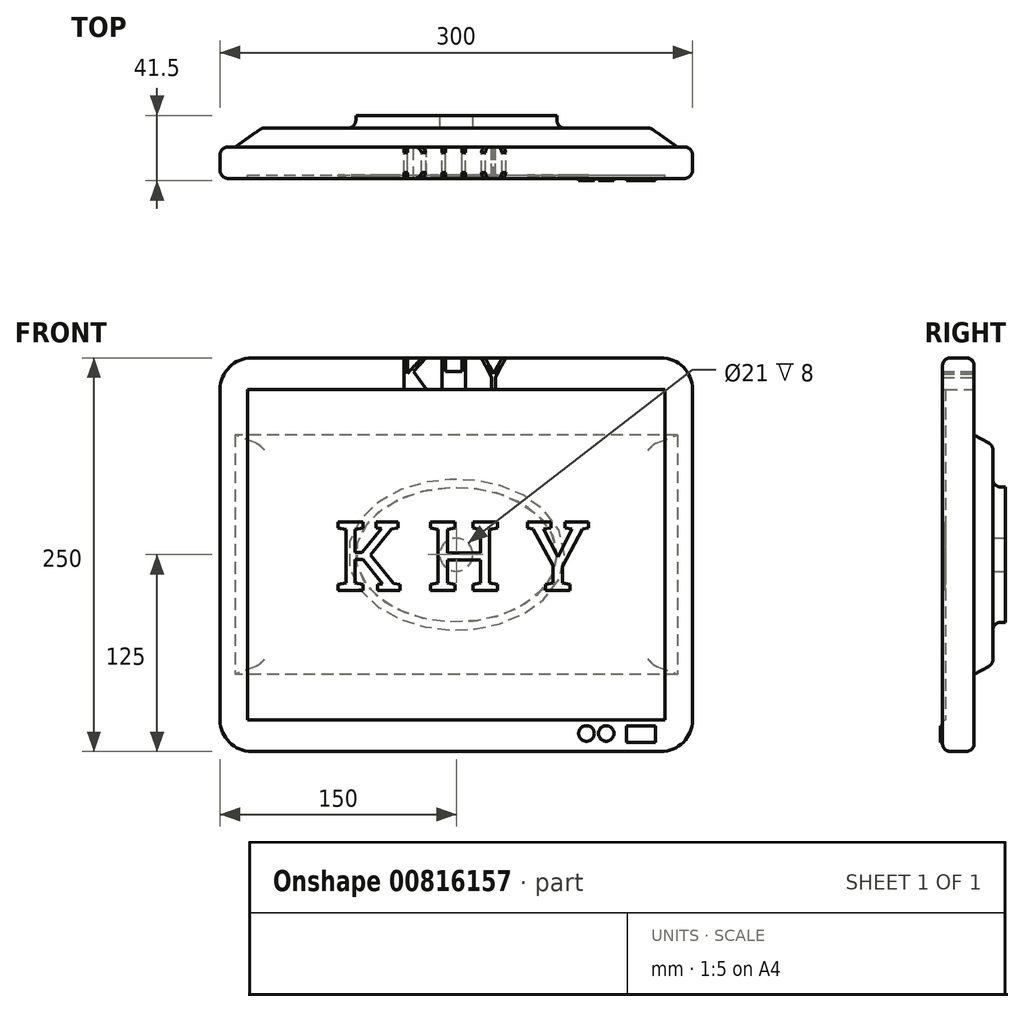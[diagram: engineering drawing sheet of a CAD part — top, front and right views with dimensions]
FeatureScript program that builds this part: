
annotation { "Feature Type Name" : "Feature", "Feature Type Description" : "" }
export const myFeature = defineFeature(function(context is Context, id is Id, definition is map)
    precondition{}
    {
        {
            var Q0;
            Q0=qCreatedBy(makeId("Front.planeOp"),FACE);
            var sketch = newSketch(context, id + "F0", { "sketchPlane" : qUnion([Q0])});
            skLineSegment(sketch, "E0.bottom", {"start": v(-130, 125) * mm, "end": v(130, 125) * mm});
            skLineSegment(sketch, "E0.top", {"start": v(-130, -125) * mm, "end": v(130, -125) * mm});
            skLineSegment(sketch, "E0.left", {"start": v(-150, 105) * mm, "end": v(-150, -105) * mm});
            skLineSegment(sketch, "E0.right", {"start": v(150, 105) * mm, "end": v(150, -105) * mm});
            skPoint(sketch, "E0.middle", {"position": v(0, 0) * mm});
            skLineSegment(sketch, "E1.bottom", {"start": v(-132.5, 105) * mm, "end": v(132.5, 105) * mm});
            skLineSegment(sketch, "E1.top", {"start": v(-132.5, -105) * mm, "end": v(132.5, -105) * mm});
            skLineSegment(sketch, "E1.left", {"start": v(-132.5, 105) * mm, "end": v(-132.5, -105) * mm});
            skLineSegment(sketch, "E1.right", {"start": v(132.5, 105) * mm, "end": v(132.5, -105) * mm});
            skPoint(sketch, "E2.visualSharp", {"position": v(-150, 125) * mm});
            skArc(sketch, "E2.filletArc", {"start": v(-130, 125) * mm, "mid": v(-144.14, 119.14) * mm, "end": v(-150, 105) * mm});
            skPoint(sketch, "E3.visualSharp", {"position": v(150, 125) * mm});
            skArc(sketch, "E3.filletArc", {"start": v(150, 105) * mm, "mid": v(144.14, 119.14) * mm, "end": v(130, 125) * mm});
            skPoint(sketch, "E4.visualSharp", {"position": v(-150, -125) * mm});
            skArc(sketch, "E4.filletArc", {"start": v(-150, -105) * mm, "mid": v(-144.14, -119.14) * mm, "end": v(-130, -125) * mm});
            skPoint(sketch, "E5.visualSharp", {"position": v(150, -125) * mm});
            skArc(sketch, "E5.filletArc", {"start": v(130, -125) * mm, "mid": v(144.14, -119.14) * mm, "end": v(150, -105) * mm});
            skText(sketch, "E6", { "text": "K H Y", "fontName": "OpenSans-Regular.ttf"});
            const initialGuessF0  = {"E6": [-0.0361, 0.105, 1, 0, 0.02]};
            skSetInitialGuess(sketch, initialGuessF0);
            skSolve(sketch);
        }
        {
            var Q0;
            Q0 = qSketchRegion(id + "F0", true);
            extrude(context, id + "F1", {"entities" : qUnion([Q0]), "depth" : 20 * mm, "offsetDistance" : 25 * mm});
        }
        {
            var Q0;
            Q0=makeQuery(id+"F0.imprint","IMPRINT",FACE,{"disambiguationData":[TD([[makeQuery(id+"F0.imprint","IMPRINT",EDGE,{"derivedFrom":sQuery(id+"F0.wireOp",EDGE,"E1.top")}),1.0]])]});
            extrude(context, id + "F2", {"entities" : qUnion([Q0]), "operationType" : NewBodyOperationType.ADD, "depth" : 18 * mm, "offsetDistance" : 25 * mm});
        }
        {
            var Q0;
            Q0=makeQuery(id+"F2.opExtrude","CAP_FACE",FACE,{"disambiguationData":[OSD([sQuery(id+"F0.wireOp",EDGE,"E1.bottom"),sQuery(id+"F0.wireOp",EDGE,"E1.top"),sQuery(id+"F0.wireOp",EDGE,"E1.left"),sQuery(id+"F0.wireOp",EDGE,"E1.right"),sQuery(id+"F0.wireOp",EDGE,"E6.sketch_text.stroke-0"),sQuery(id+"F0.wireOp",EDGE,"E6.sketch_text.stroke-4"),sQuery(id+"F0.wireOp",EDGE,"E6.sketch_text.stroke-12"),sQuery(id+"F0.wireOp",EDGE,"E6.sketch_text.stroke-16"),sQuery(id+"F0.wireOp",EDGE,"E6.sketch_text.stroke-28")])],"isStart":false});
            var sketch = newSketch(context, id + "F3", { "sketchPlane" : qUnion([Q0])});
            skText(sketch, "E7", { "text": " K H Y\n", "fontName": "RobotoSlab-Regular.ttf"});
            const initialGuessF3  = {"E7": [-0.09232, -0.02268, 1, 0, 0.044]};
            skSetInitialGuess(sketch, initialGuessF3);
            skSolve(sketch);
        }
        {
            var Q0;
            Q0 = qSketchRegion(id + "F3", true);
            extrude(context, id + "F4", {"entities" : qUnion([Q0]), "depth" : 0.5 * mm, "offsetDistance" : 25 * mm});
        }
        {
            var Q0;
            Q0=qCreatedBy(makeId("Front.planeOp"),FACE);
            cPlane(context, id + "F5", {"entities" : qUnion([Q0]), "cplaneType" : CPlaneType.OFFSET, "offset" : 12 * mm, "oppositeDirection" : true, "width" : 150 * mm, "height" : 150 * mm});
        }
        {
            var Q0;
            Q0=qCreatedBy(id+"F5.planeOp",FACE);
            var sketch = newSketch(context, id + "F6", { "sketchPlane" : qUnion([Q0])});
            skLineSegment(sketch, "E8.bottom", {"start": v(123.4, 69.44) * mm, "end": v(-123.4, 69.44) * mm});
            skLineSegment(sketch, "E8.top", {"start": v(123.4, -69.44) * mm, "end": v(-123.4, -69.44) * mm});
            skLineSegment(sketch, "E8.left", {"start": v(123.4, 69.44) * mm, "end": v(123.4, -69.44) * mm});
            skLineSegment(sketch, "E8.right", {"start": v(-123.4, 69.44) * mm, "end": v(-123.4, -69.44) * mm});
            skPoint(sketch, "E8.middle", {"position": v(0, 0) * mm});
            skSolve(sketch);
        }
        {
            var Q0;
            Q0=qCreatedBy(makeId("Front.planeOp"),FACE);
            var sketch = newSketch(context, id + "F7", { "sketchPlane" : qUnion([Q0])});
            skLineSegment(sketch, "E9.bottom", {"start": v(140.37, 75.91) * mm, "end": v(-140.37, 75.91) * mm});
            skLineSegment(sketch, "E9.top", {"start": v(140.37, -75.91) * mm, "end": v(-140.37, -75.91) * mm});
            skLineSegment(sketch, "E9.left", {"start": v(140.37, 75.91) * mm, "end": v(140.37, -75.91) * mm});
            skLineSegment(sketch, "E9.right", {"start": v(-140.37, 75.91) * mm, "end": v(-140.37, -75.91) * mm});
            skPoint(sketch, "E9.middle", {"position": v(0, 0) * mm});
            skSolve(sketch);
        }
        {
            var Q1;
            Q1=makeQuery(id+"F6.imprint","IMPRINT",FACE,{"disambiguationData":[TD([[makeQuery(id+"F6.imprint","IMPRINT",EDGE,{"derivedFrom":sQuery(id+"F6.wireOp",EDGE,"E8.bottom")}),1.0]])]});
            var Q2;
            Q2=makeQuery(id+"F7.imprint","IMPRINT",FACE,{"disambiguationData":[TD([[makeQuery(id+"F7.imprint","IMPRINT",EDGE,{"derivedFrom":sQuery(id+"F7.wireOp",EDGE,"E9.bottom")}),1.0]])]});
            loft(context, id + "F8", {"operationType" : NewBodyOperationType.ADD, "sheetProfilesArray" : [{ "sheetProfileEntities" : qUnion([Q1]) }, { "sheetProfileEntities" : qUnion([Q2]) }]});
        }
        {
            var Q0;
            Q0=makeQuery(id+"F8.opLoft","CAP_FACE",FACE,{"disambiguationData":[OSD([makeQuery(id+"F6.imprint","IMPRINT",FACE,{"disambiguationData":[TD([[makeQuery(id+"F6.imprint","IMPRINT",EDGE,{"derivedFrom":sQuery(id+"F6.wireOp",EDGE,"E8.bottom")}),1.0]])]})])],"isStart":true});
            var sketch = newSketch(context, id + "F9", { "sketchPlane" : qUnion([Q0])});
            skEllipse(sketch, "E10", {"center": v(0, 0) * mm, "majorRadius": 63.83 * mm, "minorRadius": 42.9 * mm, "majorAxis": v(-1, 0)});
            skSolve(sketch);
        }
        {
            var Q0;
            Q0 = qSketchRegion(id + "F9", true);
            extrude(context, id + "F10", {"entities" : qUnion([Q0]), "operationType" : NewBodyOperationType.ADD, "depth" : 8 * mm, "offsetDistance" : 25 * mm});
        }
        {
            var Q0;
            Q0=makeQuery(id+"F1.opExtrude","CAP_FACE",FACE,{"disambiguationData":[OSD([sQuery(id+"F0.wireOp",EDGE,"E0.bottom"),sQuery(id+"F0.wireOp",EDGE,"E0.top"),sQuery(id+"F0.wireOp",EDGE,"E0.left"),sQuery(id+"F0.wireOp",EDGE,"E0.right"),sQuery(id+"F0.wireOp",EDGE,"E1.bottom"),sQuery(id+"F0.wireOp",EDGE,"E1.top"),sQuery(id+"F0.wireOp",EDGE,"E1.left"),sQuery(id+"F0.wireOp",EDGE,"E1.right"),sQuery(id+"F0.wireOp",EDGE,"E2.filletArc"),sQuery(id+"F0.wireOp",EDGE,"E3.filletArc"),sQuery(id+"F0.wireOp",EDGE,"E4.filletArc"),sQuery(id+"F0.wireOp",EDGE,"E5.filletArc"),sQuery(id+"F0.wireOp",EDGE,"E6.sketch_text.stroke-5"),sQuery(id+"F0.wireOp",EDGE,"E6.sketch_text.stroke-6"),sQuery(id+"F0.wireOp",EDGE,"E6.sketch_text.stroke-7"),sQuery(id+"F0.wireOp",EDGE,"E6.sketch_text.stroke-8"),sQuery(id+"F0.wireOp",EDGE,"E6.sketch_text.stroke-9"),sQuery(id+"F0.wireOp",EDGE,"E6.sketch_text.stroke-10"),sQuery(id+"F0.wireOp",EDGE,"E6.sketch_text.stroke-11"),sQuery(id+"F0.wireOp",EDGE,"E6.sketch_text.stroke-17"),sQuery(id+"F0.wireOp",EDGE,"E6.sketch_text.stroke-18"),sQuery(id+"F0.wireOp",EDGE,"E6.sketch_text.stroke-19"),sQuery(id+"F0.wireOp",EDGE,"E6.sketch_text.stroke-20"),sQuery(id+"F0.wireOp",EDGE,"E6.sketch_text.stroke-21"),sQuery(id+"F0.wireOp",EDGE,"E6.sketch_text.stroke-22"),sQuery(id+"F0.wireOp",EDGE,"E6.sketch_text.stroke-23"),sQuery(id+"F0.wireOp",EDGE,"E6.sketch_text.stroke-24"),sQuery(id+"F0.wireOp",EDGE,"E6.sketch_text.stroke-25"),sQuery(id+"F0.wireOp",EDGE,"E6.sketch_text.stroke-26"),sQuery(id+"F0.wireOp",EDGE,"E6.sketch_text.stroke-27"),sQuery(id+"F0.wireOp",EDGE,"E6.sketch_text.stroke-29"),sQuery(id+"F0.wireOp",EDGE,"E6.sketch_text.stroke-30"),sQuery(id+"F0.wireOp",EDGE,"E6.sketch_text.stroke-31"),sQuery(id+"F0.wireOp",EDGE,"E6.sketch_text.stroke-32")])],"isStart":false});
            var sketch = newSketch(context, id + "F11", { "sketchPlane" : qUnion([Q0])});
            skLineSegment(sketch, "E11.bottom", {"start": v(108.18, -108.63) * mm, "end": v(126.55, -108.63) * mm});
            skLineSegment(sketch, "E11.top", {"start": v(108.18, -119.38) * mm, "end": v(126.55, -119.38) * mm});
            skLineSegment(sketch, "E11.left", {"start": v(108.18, -108.63) * mm, "end": v(108.18, -119.38) * mm});
            skLineSegment(sketch, "E11.right", {"start": v(126.55, -108.63) * mm, "end": v(126.55, -119.38) * mm});
            skCircle(sketch, "E12", {"center": v(95.19, -113.56) * mm, "radius": 4.93 * mm});
            skCircle(sketch, "E13", {"center": v(82.65, -113.56) * mm, "radius": 4.95 * mm});
            skSolve(sketch);
        }
        {
            var Q0;
            Q0 = qSketchRegion(id + "F11", true);
            extrude(context, id + "F12", {"entities" : qUnion([Q0]), "operationType" : NewBodyOperationType.ADD, "depth" : 1.5 * mm, "offsetDistance" : 25 * mm});
        }
        {
            var Q0;
            Q0=makeQuery(id+"F8.opLoft","CAP_FACE",FACE,{"disambiguationData":[OSD([makeQuery(id+"F6.imprint","IMPRINT",FACE,{"disambiguationData":[TD([[makeQuery(id+"F6.imprint","IMPRINT",EDGE,{"derivedFrom":sQuery(id+"F6.wireOp",EDGE,"E8.bottom")}),1.0]])]})])],"isStart":true});
            var Q1;
            Q1=makeQuery(id+"F1.opExtrude","CAP_EDGE",EDGE,{"disambiguationData":[OSD([sQuery(id+"F0.wireOp",EDGE,"E0.right")])],"isStart":true});
            var Q2;
            Q2=makeQuery(id+"F1.opExtrude","CAP_EDGE",EDGE,{"disambiguationData":[OSD([sQuery(id+"F0.wireOp",EDGE,"E0.top")])],"isStart":false});
            fillet(context, id + "F13", {"entities" : qUnion([Q0, Q1, Q2]), "radius" : 5 * mm, "tangentPropagation" : true, "allowEdgeOverflow" : false});
        }
        {
            var Q0;
            Q0=makeQuery(id+"F10.opExtrude","CAP_FACE",FACE,{"disambiguationData":[OSD([sQuery(id+"F9.wireOp",EDGE,"E10")])],"isStart":false});
            var sketch = newSketch(context, id + "F14", { "sketchPlane" : qUnion([Q0])});
            skCircle(sketch, "E14", {"center": v(0, 0) * mm, "radius": 10.5 * mm});
            skSolve(sketch);
        }
        {
            var Q0;
            Q0 = qSketchRegion(id + "F14", true);
            extrude(context, id + "F15", {"entities" : qUnion([Q0]), "operationType" : NewBodyOperationType.REMOVE, "oppositeDirection" : true, "depth" : 8 * mm, "offsetDistance" : 25 * mm});
        }
    });
